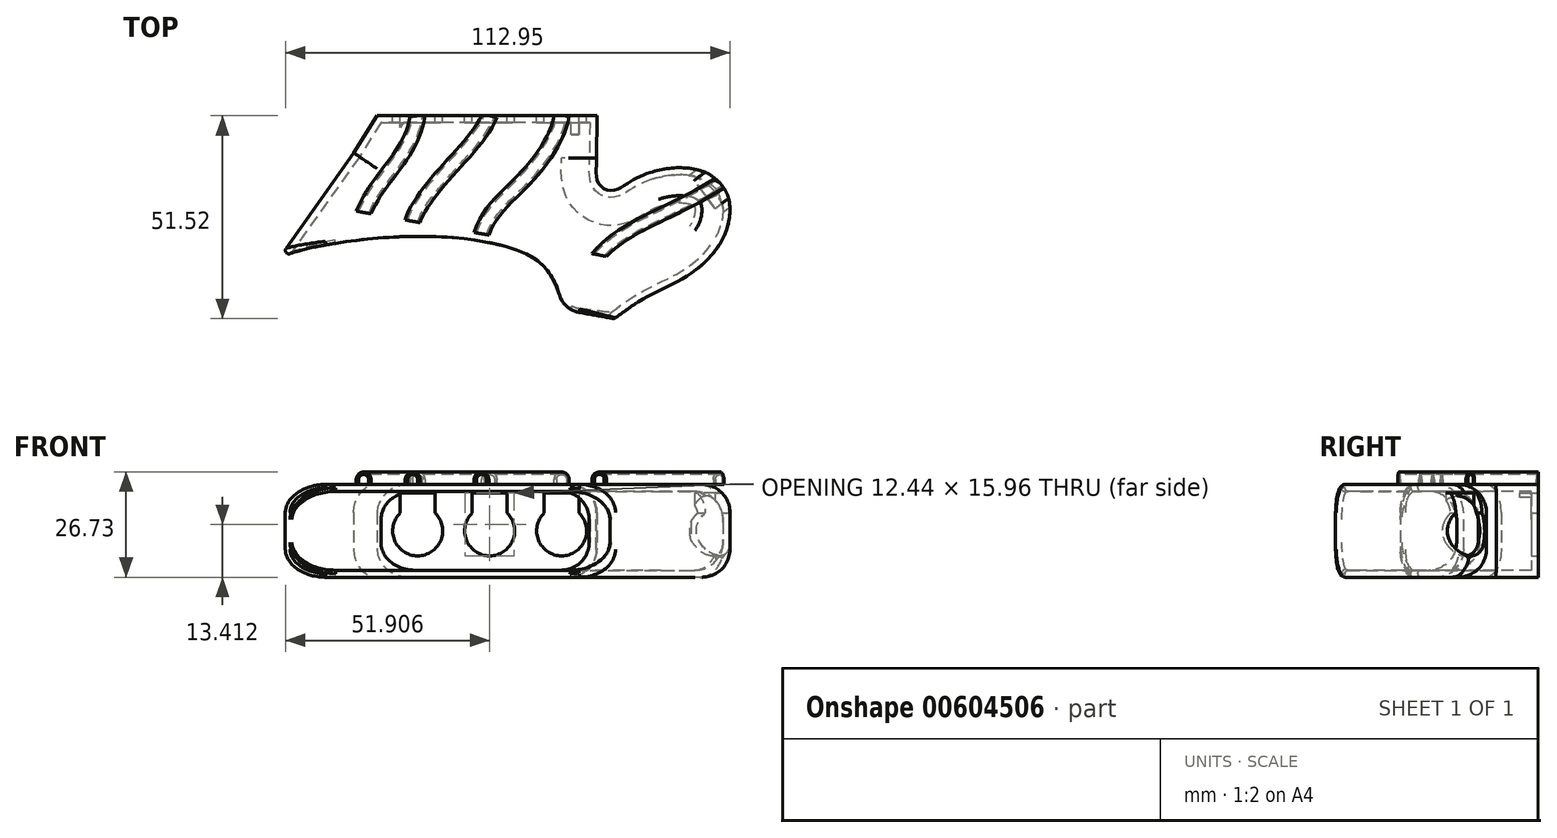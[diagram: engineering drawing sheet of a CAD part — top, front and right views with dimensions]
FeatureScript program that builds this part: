
annotation { "Feature Type Name" : "Feature", "Feature Type Description" : "" }
export const myFeature = defineFeature(function(context is Context, id is Id, definition is map)
    precondition{}
    {
        {
            var Q0;
            Q0=qCreatedBy(makeId("Top.planeOp"),FACE);
            var sketch = newSketch(context, id + "F0", { "sketchPlane" : qUnion([Q0])});
            skLineSegment(sketch, "E0", {"start": v(-2.53, 3.76) * mm, "end": v(-21.5, -22.97) * mm});
            skLineSegment(sketch, "E1", {"start": v(54.7, -36.74) * mm, "end": v(63.69, -38.36) * mm});
            skFitSpline(sketch, "E2", {"points": [v(54.7, 11.38) * mm, v(59, 4.04) * mm, v(59.53, -3.66) * mm, v(63.11, -5.79) * mm, v(68.43, -3.13) * mm, v(80.08, 0) * mm, v(90.97, -4.14) * mm, v(92.29, -15.51) * mm, v(83.28, -26.78) * mm, v(72.06, -32.72) * mm, v(63.69, -38.36) * mm], "startDerivative": vector(65.3, -76.98) * mm, "endDerivative": vector(-77.9, -55.9) * mm});
            skLineSegment(sketch, "E3", {"start": v(59.3, 13.2) * mm, "end": v(3.43, 13.2) * mm});
            skLineSegment(sketch, "E4", {"start": v(3.43, 13.2) * mm, "end": v(-2.53, 3.76) * mm});
            skLineSegment(sketch, "E5", {"start": v(59.3, 13.2) * mm, "end": v(59.13, 2.47) * mm});
            skLineSegment(sketch, "E6", {"start": v(84.86, 3.75) * mm, "end": v(96.23, -11.53) * mm});
            skLineSegment(sketch, "E7", {"start": v(84.86, 3.75) * mm, "end": v(72.77, -1.24) * mm});
            skLineSegment(sketch, "E8", {"start": v(96.23, -11.53) * mm, "end": v(90.2, -19.8) * mm});
            skFitSpline(sketch, "E9", {"points": [v(-21.5, -22.97) * mm, v(-10.47, -19.77) * mm, v(16.08, -17.45) * mm, v(40.88, -21.74) * mm, v(47.96, -28) * mm, v(50.62, -36) * mm], "startDerivative": vector(55.83, 25.77) * mm, "endDerivative": vector(10.05, -54.75) * mm});
            skArc(sketch, "E10.filletArc", {"start": v(49.75, -32.32) * mm, "mid": v(51.6, -35.23) * mm, "end": v(54.7, -36.74) * mm});
            skSolve(sketch);
        }
        {
            var Q0;
            Q0=makeQuery(id+"F0.imprint","IMPRINT",FACE,{"disambiguationData":[TD([[makeQuery(id+"F0.imprint","IMPRINT",EDGE,{"derivedFrom":sQuery(id+"F0.wireOp",EDGE,"E0")}),1.0]])]});
            extrude(context, id + "F1", {"entities" : qUnion([Q0]), "depth" : 23.56 * mm, "offsetDistance" : 25.4 * mm});
        }
        {
            var Q0;
            Q0=makeQuery(id+"F1.opExtrude","SWEPT_FACE",FACE,{"disambiguationData":[OSD([sQuery(id+"F0.wireOp",EDGE,"E1")])]});
            var Q1;
            Q1=makeQuery(id+"F1.opExtrude","SWEPT_FACE",FACE,{"disambiguationData":[OSD([sQuery(id+"F0.wireOp",EDGE,"E9")])]});
            var Q2;
            Q2=makeQuery(id+"F1.opExtrude","SWEPT_FACE",FACE,{"disambiguationData":[OSD([sQuery(id+"F0.wireOp",EDGE,"E10.filletArc")])]});
            shell(context, id + "F2", {"entities" : qUnion([Q0, Q1, Q2]), "thickness" : 1.78 * mm});
        }
        {
            var Q0;
            {var subQ0=sQuery(id+"F0.wireOp",EDGE,"E2");Q0=makeQuery(id+"F2.opShell","OFFSET_EDGE",EDGE,{"disambiguationData":[OSD([subQ0]),TDD([makeQuery(id+"F1.opExtrude","CAP_EDGE",EDGE,{"disambiguationData":[OSD([subQ0])],"isStart":false})])]});}
            var Q1;
            {var subQ0=sQuery(id+"F0.wireOp",EDGE,"E0");Q1=makeQuery(id+"F2.opShell","OFFSET_EDGE",EDGE,{"disambiguationData":[OSD([subQ0]),TDD([makeQuery(id+"F1.opExtrude","CAP_EDGE",EDGE,{"disambiguationData":[OSD([subQ0])],"isStart":true})])]});}
            var Q2;
            {var subQ0=sQuery(id+"F0.wireOp",EDGE,"E0");Q2=makeQuery(id+"F2.opShell","OFFSET_EDGE",EDGE,{"disambiguationData":[OSD([subQ0]),TDD([makeQuery(id+"F1.opExtrude","CAP_EDGE",EDGE,{"disambiguationData":[OSD([subQ0])],"isStart":false})])]});}
            var Q3;
            Q3=makeQuery(id+"F2.opShell","OFFSET_EDGE",EDGE,{"disambiguationData":[OSD([sQuery(id+"F0.wireOp",EDGE,"E0"),sQuery(id+"F0.wireOp",EDGE,"E4")])]});
            var Q4;
            {var subQ0=sQuery(id+"F0.wireOp",EDGE,"E4");Q4=makeQuery(id+"F2.opShell","OFFSET_EDGE",EDGE,{"disambiguationData":[OSD([subQ0]),TDD([makeQuery(id+"F1.opExtrude","CAP_EDGE",EDGE,{"disambiguationData":[OSD([subQ0])],"isStart":false})])]});}
            var Q5;
            {var subQ0=sQuery(id+"F0.wireOp",EDGE,"E4");Q5=makeQuery(id+"F2.opShell","OFFSET_EDGE",EDGE,{"disambiguationData":[OSD([subQ0]),TDD([makeQuery(id+"F1.opExtrude","CAP_EDGE",EDGE,{"disambiguationData":[OSD([subQ0])],"isStart":true})])]});}
            var Q6;
            Q6=makeQuery(id+"F1.opExtrude","CAP_EDGE",EDGE,{"disambiguationData":[OSD([sQuery(id+"F0.wireOp",EDGE,"E2")])],"isStart":false});
            var Q7;
            Q7=makeQuery(id+"F1.opExtrude","CAP_EDGE",EDGE,{"disambiguationData":[OSD([sQuery(id+"F0.wireOp",EDGE,"E0")])],"isStart":false});
            var Q8;
            Q8=makeQuery(id+"F1.opExtrude","CAP_EDGE",EDGE,{"disambiguationData":[OSD([sQuery(id+"F0.wireOp",EDGE,"E4")])],"isStart":false});
            var Q9;
            Q9=makeQuery(id+"F1.opExtrude","CAP_EDGE",EDGE,{"disambiguationData":[OSD([sQuery(id+"F0.wireOp",EDGE,"E2")])],"isStart":true});
            var Q10;
            Q10=makeQuery(id+"F1.opExtrude","CAP_EDGE",EDGE,{"disambiguationData":[OSD([sQuery(id+"F0.wireOp",EDGE,"E0")])],"isStart":true});
            var Q11;
            Q11=makeQuery(id+"F1.opExtrude","CAP_EDGE",EDGE,{"disambiguationData":[OSD([sQuery(id+"F0.wireOp",EDGE,"E5")])],"isStart":false});
            var Q12;
            Q12=makeQuery(id+"F1.opExtrude","CAP_EDGE",EDGE,{"disambiguationData":[OSD([sQuery(id+"F0.wireOp",EDGE,"E5")])],"isStart":true});
            var Q13;
            {var subQ0=sQuery(id+"F0.wireOp",EDGE,"E5");Q13=makeQuery(id+"F2.opShell","OFFSET_EDGE",EDGE,{"disambiguationData":[OSD([subQ0]),TDD([makeQuery(id+"F1.opExtrude","CAP_EDGE",EDGE,{"disambiguationData":[OSD([subQ0])],"isStart":false})])]});}
            var Q14;
            {var subQ0=sQuery(id+"F0.wireOp",EDGE,"E5");Q14=makeQuery(id+"F2.opShell","OFFSET_EDGE",EDGE,{"disambiguationData":[OSD([subQ0]),TDD([makeQuery(id+"F1.opExtrude","CAP_EDGE",EDGE,{"disambiguationData":[OSD([subQ0])],"isStart":true})])]});}
            var Q15;
            Q15=makeQuery(id+"F1.opExtrude","CAP_EDGE",EDGE,{"disambiguationData":[OSD([sQuery(id+"F0.wireOp",EDGE,"E4")])],"isStart":true});
            var Q16;
            {var subQ0=sQuery(id+"F0.wireOp",EDGE,"E2");Q16=makeQuery(id+"F2.opShell","OFFSET_EDGE",EDGE,{"disambiguationData":[OSD([subQ0]),TDD([makeQuery(id+"F1.opExtrude","CAP_EDGE",EDGE,{"disambiguationData":[OSD([subQ0])],"isStart":false})])]});}
            var Q17;
            {var subQ0=sQuery(id+"F0.wireOp",EDGE,"E8");Q17=makeQuery(id+"F2.opShell","OFFSET_EDGE",EDGE,{"disambiguationData":[OSD([subQ0]),TDD([makeQuery(id+"F1.opExtrude","CAP_EDGE",EDGE,{"disambiguationData":[OSD([subQ0])],"isStart":false})])]});}
            var Q18;
            {var subQ0=sQuery(id+"F0.wireOp",EDGE,"E2");Q18=makeQuery(id+"F2.opShell","OFFSET_EDGE",EDGE,{"disambiguationData":[OSD([subQ0]),TDD([makeQuery(id+"F1.opExtrude","CAP_EDGE",EDGE,{"disambiguationData":[OSD([subQ0])],"isStart":true})])]});}
            var Q19;
            {var subQ0=sQuery(id+"F0.wireOp",EDGE,"E8");Q19=makeQuery(id+"F2.opShell","OFFSET_EDGE",EDGE,{"disambiguationData":[OSD([subQ0]),TDD([makeQuery(id+"F1.opExtrude","CAP_EDGE",EDGE,{"disambiguationData":[OSD([subQ0])],"isStart":true})])]});}
            var Q20;
            {var subQ0=sQuery(id+"F0.wireOp",EDGE,"E7");Q20=makeQuery(id+"F2.opShell","OFFSET_EDGE",EDGE,{"disambiguationData":[OSD([subQ0]),TDD([makeQuery(id+"F1.opExtrude","CAP_EDGE",EDGE,{"disambiguationData":[OSD([subQ0])],"isStart":false})])]});}
            var Q21;
            {var subQ0=sQuery(id+"F0.wireOp",EDGE,"E7");Q21=makeQuery(id+"F2.opShell","OFFSET_EDGE",EDGE,{"disambiguationData":[OSD([subQ0]),TDD([makeQuery(id+"F1.opExtrude","CAP_EDGE",EDGE,{"disambiguationData":[OSD([subQ0])],"isStart":true})])]});}
            var Q22;
            Q22=makeQuery(id+"F1.opExtrude","CAP_EDGE",EDGE,{"disambiguationData":[OSD([sQuery(id+"F0.wireOp",EDGE,"E7")])],"isStart":true});
            var Q23;
            Q23=makeQuery(id+"F1.opExtrude","CAP_EDGE",EDGE,{"disambiguationData":[OSD([sQuery(id+"F0.wireOp",EDGE,"E2")])],"isStart":false});
            var Q24;
            Q24=makeQuery(id+"F1.opExtrude","CAP_EDGE",EDGE,{"disambiguationData":[OSD([sQuery(id+"F0.wireOp",EDGE,"E8")])],"isStart":false});
            var Q25;
            Q25=makeQuery(id+"F1.opExtrude","CAP_EDGE",EDGE,{"disambiguationData":[OSD([sQuery(id+"F0.wireOp",EDGE,"E8")])],"isStart":true});
            var Q26;
            Q26=makeQuery(id+"F1.opExtrude","CAP_EDGE",EDGE,{"disambiguationData":[OSD([sQuery(id+"F0.wireOp",EDGE,"E2")])],"isStart":true});
            var Q27;
            Q27=makeQuery(id+"F1.opExtrude","CAP_EDGE",EDGE,{"disambiguationData":[OSD([sQuery(id+"F0.wireOp",EDGE,"E7")])],"isStart":false});
            fillet(context, id + "F3", {"entities" : qUnion([Q0, Q1, Q2, Q3, Q4, Q5, Q6, Q7, Q8, Q9, Q10, Q11, Q12, Q13, Q14, Q15, Q16, Q17, Q18, Q19, Q20, Q21, Q22, Q23, Q24, Q25, Q26, Q27]), "radius" : 7.11 * mm, "tangentPropagation" : true, "allowEdgeOverflow" : false});
        }
        {
            var Q0;
            Q0=makeQuery(id+"F1.opExtrude","SWEPT_FACE",FACE,{"disambiguationData":[OSD([sQuery(id+"F0.wireOp",EDGE,"E3")])]});
            var sketch = newSketch(context, id + "F4", { "sketchPlane" : qUnion([Q0])});
            skCircle(sketch, "E11", {"center": v(-32.02, 11.78) * mm, "radius": 6.35 * mm});
            skCircle(sketch, "E12", {"center": v(-50.3, 11.78) * mm, "radius": 6.35 * mm});
            skCircle(sketch, "E13.MirrorC", {"center": v(-13.73, 11.78) * mm, "radius": 6.35 * mm});
            skLineSegment(sketch, "E14", {"start": v(-32.02, 0) * mm, "end": v(-32.02, 23.56) * mm});
            skSolve(sketch);
        }
        {
            var Q0;
            Q0=qSketchRegion(id+"F4",true);
            extrude(context, id + "F5", {"entities" : qUnion([Q0]), "operationType" : NewBodyOperationType.REMOVE, "endBound" : BoundingType.THROUGH_ALL, "oppositeDirection" : true, "depth" : 25.4 * mm, "offsetDistance" : 25.4 * mm});
        }
        {
            var Q0;
            Q0=makeQuery(id+"F1.opExtrude","SWEPT_FACE",FACE,{"disambiguationData":[OSD([sQuery(id+"F0.wireOp",EDGE,"E3")])]});
            var sketch = newSketch(context, id + "F6", { "sketchPlane" : qUnion([Q0])});
            skLineSegment(sketch, "E15", {"start": v(-32.02, 23.56) * mm, "end": v(-32.02, 0) * mm});
            skLineSegment(sketch, "E16", {"start": v(-32.02, 21.4) * mm, "end": v(-27.57, 21.4) * mm});
            skLineSegment(sketch, "E17", {"start": v(-27.57, 21.4) * mm, "end": v(-27.57, 16.31) * mm});
            skArc(sketch, "E18", {"start": v(-32.02, 18.13) * mm, "mid": v(-29.62, 17.66) * mm, "end": v(-27.57, 16.31) * mm});
            skArc(sketch, "E19.MirrorCS", {"start": v(-32.02, 18.13) * mm, "mid": v(-34.42, 17.66) * mm, "end": v(-36.46, 16.31) * mm});
            skLineSegment(sketch, "E20.MirrorCS", {"start": v(-32.02, 21.4) * mm, "end": v(-36.46, 21.4) * mm});
            skLineSegment(sketch, "E21.MirrorCS", {"start": v(-36.46, 21.4) * mm, "end": v(-36.46, 16.31) * mm});
            skLineSegment(sketch, "E22", {"start": v(-50.3, 21.4) * mm, "end": v(-45.86, 21.4) * mm});
            skLineSegment(sketch, "E23", {"start": v(-45.86, 21.4) * mm, "end": v(-45.86, 16.31) * mm});
            skArc(sketch, "E24", {"start": v(-50.3, 18.13) * mm, "mid": v(-47.9, 17.66) * mm, "end": v(-45.86, 16.31) * mm});
            skArc(sketch, "E25.MirrorCS", {"start": v(-50.3, 18.13) * mm, "mid": v(-52.7, 17.66) * mm, "end": v(-54.75, 16.31) * mm});
            skLineSegment(sketch, "E26.MirrorCS", {"start": v(-50.3, 21.4) * mm, "end": v(-54.75, 21.4) * mm});
            skLineSegment(sketch, "E27.MirrorCS", {"start": v(-54.75, 21.4) * mm, "end": v(-54.75, 16.31) * mm});
            skLineSegment(sketch, "E28", {"start": v(-13.73, 21.4) * mm, "end": v(-9.28, 21.4) * mm});
            skLineSegment(sketch, "E29", {"start": v(-9.28, 21.4) * mm, "end": v(-9.28, 16.31) * mm});
            skArc(sketch, "E30", {"start": v(-13.73, 18.13) * mm, "mid": v(-11.33, 17.66) * mm, "end": v(-9.28, 16.31) * mm});
            skArc(sketch, "E31.MirrorCS", {"start": v(-13.73, 18.13) * mm, "mid": v(-16.13, 17.66) * mm, "end": v(-18.17, 16.31) * mm});
            skLineSegment(sketch, "E32.MirrorCS", {"start": v(-13.73, 21.4) * mm, "end": v(-18.17, 21.4) * mm});
            skLineSegment(sketch, "E33.MirrorCS", {"start": v(-18.17, 21.4) * mm, "end": v(-18.17, 16.31) * mm});
            skSolve(sketch);
        }
        {
            var Q0;
            Q0=qSketchRegion(id+"F6",true);
            extrude(context, id + "F7", {"entities" : qUnion([Q0]), "operationType" : NewBodyOperationType.REMOVE, "oppositeDirection" : true, "depth" : 4.83 * mm, "offsetDistance" : 25.4 * mm});
        }
        {
            var Q0;
            Q0=makeQuery(id+"F1.opExtrude","SWEPT_FACE",FACE,{"disambiguationData":[OSD([sQuery(id+"F0.wireOp",EDGE,"E6")])]});
            var sketch = newSketch(context, id + "F8", { "sketchPlane" : qUnion([Q0])});
            skCircle(sketch, "E34", {"center": v(-57.18, 11.78) * mm, "radius": 6.35 * mm});
            skLineSegment(sketch, "E35", {"start": v(-57.18, 21.4) * mm, "end": v(-52.74, 21.4) * mm});
            skLineSegment(sketch, "E36", {"start": v(-52.74, 21.4) * mm, "end": v(-52.74, 16.31) * mm});
            skLineSegment(sketch, "E37.MirrorCS", {"start": v(-57.18, 21.4) * mm, "end": v(-61.63, 21.4) * mm});
            skLineSegment(sketch, "E38.MirrorCS", {"start": v(-61.63, 21.4) * mm, "end": v(-61.63, 16.31) * mm});
            skSolve(sketch);
        }
        {
            var Q0;
            Q0 = qSketchRegion(id + "F8", true);
            var Q1;
            Q1=makeQuery(id+"F8.imprint","IMPRINT",FACE,{"disambiguationData":[TD([[makeQuery(id+"F8.imprint","IMPRINT",EDGE,{"derivedFrom":sQuery(id+"F8.wireOp",EDGE,"E35")}),-1.0]])]});
            var Q2;
            {var subQ0=sQuery(id+"F8.wireOp",EDGE,"E34");var subQ1=makeQuery(id+"F8.imprint","INTERSECT",VERTEX,{"derivedFrom":[subQ0,sQuery(id+"F8.wireOp",EDGE,"E36")]});Q2=makeQuery(id+"F8.imprint","IMPRINT",FACE,{"disambiguationData":[TD([[makeQuery(id+"F8.imprint","IMPRINT",EDGE,{"disambiguationData":[TD([[subQ1,-1.0]])],"derivedFrom":subQ0}),1.0]])]});}
            extrude(context, id + "F9", {"entities" : qUnion([Q0, Q1, Q2]), "operationType" : NewBodyOperationType.REMOVE, "oppositeDirection" : true, "depth" : 4.83 * mm, "offsetDistance" : 25.4 * mm});
        }
        {
            var Q0;
            Q0=makeQuery(id+"F1.opExtrude","CAP_FACE",FACE,{"disambiguationData":[OSD([sQuery(id+"F0.wireOp",EDGE,"E0"),sQuery(id+"F0.wireOp",EDGE,"E1"),sQuery(id+"F0.wireOp",EDGE,"E2"),sQuery(id+"F0.wireOp",EDGE,"E3"),sQuery(id+"F0.wireOp",EDGE,"E4"),sQuery(id+"F0.wireOp",EDGE,"E5"),sQuery(id+"F0.wireOp",EDGE,"E6"),sQuery(id+"F0.wireOp",EDGE,"E7"),sQuery(id+"F0.wireOp",EDGE,"E8"),sQuery(id+"F0.wireOp",EDGE,"E2"),sQuery(id+"F0.wireOp",EDGE,"E9"),sQuery(id+"F0.wireOp",EDGE,"E10.filletArc")])],"isStart":false});
            var sketch = newSketch(context, id + "F10", { "sketchPlane" : qUnion([Q0])});
            skPoint(sketch, "E39.0", {"position": v(-1.92, -11.02) * mm});
            skPoint(sketch, "E40.0", {"position": v(61.78, -22.53) * mm});
            skLineSegment(sketch, "E41", {"start": v(-1.92, -11.02) * mm, "end": v(61.78, -22.53) * mm});
            skPoint(sketch, "E42.0", {"position": v(13.73, 13.2) * mm});
            skPoint(sketch, "E43.0", {"position": v(32.02, 13.2) * mm});
            skPoint(sketch, "E44.0", {"position": v(50.3, 13.2) * mm});
            skPoint(sketch, "E45.0", {"position": v(90.54, -3.89) * mm});
            skFitSpline(sketch, "E46", {"points": [v(13.73, 13.2) * mm, v(7.28, 0) * mm, v(0, -11.37) * mm], "startDerivative": vector(-4.34, -30.73) * mm, "endDerivative": vector(-13.54, -30.47) * mm});
            skPoint(sketch, "E47.0", {"position": v(12.45, -13.62) * mm});
            skPoint(sketch, "E48.0", {"position": v(29.95, -16.78) * mm});
            skFitSpline(sketch, "E49", {"points": [v(32.02, 13.2) * mm, v(21.18, -0.88) * mm, v(12.45, -13.62) * mm], "startDerivative": vector(-10.72, -26.08) * mm, "endDerivative": vector(-7.14, -23.27) * mm});
            skFitSpline(sketch, "E50", {"points": [v(50.3, 13.2) * mm, v(41.19, -2.5) * mm, v(29.95, -16.78) * mm], "startDerivative": vector(-5.49, -32.55) * mm, "endDerivative": vector(-12.27, -36.66) * mm});
            skFitSpline(sketch, "E51", {"points": [v(90.54, -3.89) * mm, v(72.14, -13.57) * mm, v(59.87, -22.19) * mm], "startDerivative": vector(-34.13, -21.6) * mm, "endDerivative": vector(-22.86, -25.58) * mm});
            skSolve(sketch);
        }
        {
            var Q0;
            Q0=sQuery(id+"F10.wireOp",EDGE,"E41");
            cPlane(context, id + "F11", {"entities" : qUnion([Q0]), "cplaneType" : CPlaneType.LINE_ANGLE, "offset" : 25.4 * mm, "angle" : 0 * degree, "width" : 152.4 * mm, "height" : 152.4 * mm});
        }
        {
            var Q0;
            Q0=qCreatedBy(id+"F11.planeOp",FACE);
            var sketch = newSketch(context, id + "F12", { "sketchPlane" : qUnion([Q0])});
            skPoint(sketch, "E52.0", {"position": v(-2.02, 23.56) * mm});
            skPoint(sketch, "E53.0", {"position": v(-14.67, 23.56) * mm});
            skPoint(sketch, "E54.0", {"position": v(-32.45, 23.56) * mm});
            skPoint(sketch, "E55.0", {"position": v(-62.86, 23.56) * mm});
            skLineSegment(sketch, "E56", {"start": v(-0.12, 24.83) * mm, "end": v(-0.12, 23.56) * mm});
            skLineSegment(sketch, "E57", {"start": v(-0.12, 23.56) * mm, "end": v(-3.93, 23.56) * mm});
            skLineSegment(sketch, "E58", {"start": v(-3.93, 23.56) * mm, "end": v(-3.93, 24.83) * mm});
            skLineSegment(sketch, "E59", {"start": v(-12.77, 24.83) * mm, "end": v(-12.77, 23.56) * mm});
            skLineSegment(sketch, "E60", {"start": v(-12.77, 23.56) * mm, "end": v(-16.58, 23.56) * mm});
            skLineSegment(sketch, "E61", {"start": v(-16.58, 23.56) * mm, "end": v(-16.58, 24.83) * mm});
            skLineSegment(sketch, "E62", {"start": v(-30.55, 24.83) * mm, "end": v(-30.55, 23.56) * mm});
            skLineSegment(sketch, "E63", {"start": v(-30.55, 23.56) * mm, "end": v(-34.36, 23.56) * mm});
            skLineSegment(sketch, "E64", {"start": v(-34.36, 23.56) * mm, "end": v(-34.36, 24.83) * mm});
            skLineSegment(sketch, "E65", {"start": v(-60.96, 24.83) * mm, "end": v(-60.96, 23.56) * mm});
            skLineSegment(sketch, "E66", {"start": v(-60.96, 23.56) * mm, "end": v(-64.77, 23.56) * mm});
            skLineSegment(sketch, "E67", {"start": v(-64.77, 23.56) * mm, "end": v(-64.77, 24.83) * mm});
            skArc(sketch, "E68", {"start": v(-60.96, 24.83) * mm, "mid": v(-62.86, 26.73) * mm, "end": v(-64.77, 24.83) * mm});
            skArc(sketch, "E69", {"start": v(-30.55, 24.83) * mm, "mid": v(-32.45, 26.73) * mm, "end": v(-34.36, 24.83) * mm});
            skArc(sketch, "E70", {"start": v(-12.77, 24.83) * mm, "mid": v(-14.67, 26.73) * mm, "end": v(-16.58, 24.83) * mm});
            skArc(sketch, "E71", {"start": v(-0.12, 24.83) * mm, "mid": v(-2.02, 26.73) * mm, "end": v(-3.93, 24.83) * mm});
            skLineSegment(sketch, "E72", {"start": v(-0.75, 24.83) * mm, "end": v(-0.75, 23.56) * mm});
            skLineSegment(sketch, "E73", {"start": v(-3.3, 24.83) * mm, "end": v(-3.3, 23.56) * mm});
            skArc(sketch, "E74", {"start": v(-0.75, 24.83) * mm, "mid": v(-2.02, 26.1) * mm, "end": v(-3.3, 24.83) * mm});
            skArc(sketch, "E75", {"start": v(-13.4, 24.83) * mm, "mid": v(-14.67, 26.1) * mm, "end": v(-15.94, 24.83) * mm});
            skArc(sketch, "E76", {"start": v(-31.18, 24.83) * mm, "mid": v(-32.45, 26.1) * mm, "end": v(-33.72, 24.83) * mm});
            skArc(sketch, "E77", {"start": v(-61.6, 24.83) * mm, "mid": v(-62.86, 26.1) * mm, "end": v(-64.13, 24.83) * mm});
            skLineSegment(sketch, "E78", {"start": v(-64.13, 24.83) * mm, "end": v(-64.13, 23.56) * mm});
            skLineSegment(sketch, "E79", {"start": v(-61.6, 24.83) * mm, "end": v(-61.6, 23.56) * mm});
            skLineSegment(sketch, "E80", {"start": v(-33.72, 24.83) * mm, "end": v(-33.72, 23.56) * mm});
            skLineSegment(sketch, "E81", {"start": v(-31.18, 24.83) * mm, "end": v(-31.18, 23.56) * mm});
            skLineSegment(sketch, "E82", {"start": v(-15.94, 24.83) * mm, "end": v(-15.94, 23.56) * mm});
            skLineSegment(sketch, "E83", {"start": v(-13.4, 24.83) * mm, "end": v(-13.4, 23.56) * mm});
            skSolve(sketch);
        }
        {
            var Q0;
            {var subQ3=sQuery(id+"F12.wireOp",EDGE,"E56");Q0=makeQuery(id+"F12.imprint","IMPRINT",FACE,{"disambiguationData":[TD([[makeQuery(id+"F12.imprint","IMPRINT",EDGE,{"derivedFrom":subQ3}),-1.0]])]});}
            var Q1;
            Q1=sQuery(id+"F10.wireOp",EDGE,"E46");
            sweep(context, id + "F13", {"operationType" : NewBodyOperationType.ADD, "profiles" : qUnion([Q0]), "path" : qUnion([Q1])});
        }
        {
            var Q0;
            {var subQ3=sQuery(id+"F12.wireOp",EDGE,"E59");Q0=makeQuery(id+"F12.imprint","IMPRINT",FACE,{"disambiguationData":[TD([[makeQuery(id+"F12.imprint","IMPRINT",EDGE,{"derivedFrom":subQ3}),-1.0]])]});}
            var Q1;
            Q1=sQuery(id+"F10.wireOp",EDGE,"E49");
            sweep(context, id + "F14", {"operationType" : NewBodyOperationType.ADD, "profiles" : qUnion([Q0]), "path" : qUnion([Q1])});
        }
        {
            var Q0;
            {var subQ3=sQuery(id+"F12.wireOp",EDGE,"E62");Q0=makeQuery(id+"F12.imprint","IMPRINT",FACE,{"disambiguationData":[TD([[makeQuery(id+"F12.imprint","IMPRINT",EDGE,{"derivedFrom":subQ3}),-1.0]])]});}
            var Q1;
            Q1=sQuery(id+"F10.wireOp",EDGE,"E50");
            sweep(context, id + "F15", {"operationType" : NewBodyOperationType.ADD, "profiles" : qUnion([Q0]), "path" : qUnion([Q1])});
        }
        {
            var Q0;
            {var subQ3=sQuery(id+"F12.wireOp",EDGE,"E65");Q0=makeQuery(id+"F12.imprint","IMPRINT",FACE,{"disambiguationData":[TD([[makeQuery(id+"F12.imprint","IMPRINT",EDGE,{"derivedFrom":subQ3}),-1.0]])]});}
            var Q1;
            Q1=sQuery(id+"F10.wireOp",EDGE,"E51");
            sweep(context, id + "F16", {"operationType" : NewBodyOperationType.ADD, "profiles" : qUnion([Q0]), "path" : qUnion([Q1])});
        }
        {
            var Q0;
            Q0=makeQuery(id+"F1.opExtrude","CAP_FACE",FACE,{"disambiguationData":[OSD([sQuery(id+"F0.wireOp",EDGE,"E0"),sQuery(id+"F0.wireOp",EDGE,"E1"),sQuery(id+"F0.wireOp",EDGE,"E2"),sQuery(id+"F0.wireOp",EDGE,"E3"),sQuery(id+"F0.wireOp",EDGE,"E4"),sQuery(id+"F0.wireOp",EDGE,"E5"),sQuery(id+"F0.wireOp",EDGE,"E6"),sQuery(id+"F0.wireOp",EDGE,"E7"),sQuery(id+"F0.wireOp",EDGE,"E8"),sQuery(id+"F0.wireOp",EDGE,"E2"),sQuery(id+"F0.wireOp",EDGE,"E9"),sQuery(id+"F0.wireOp",EDGE,"E10.filletArc")])],"isStart":false});
            var sketch = newSketch(context, id + "F17", { "sketchPlane" : qUnion([Q0])});
            skPoint(sketch, "E84.0", {"position": v(13.73, 13.2) * mm});
            skPoint(sketch, "E85.0", {"position": v(50.3, 13.2) * mm});
            skPoint(sketch, "E86.0", {"position": v(90.54, -3.89) * mm});
            skPoint(sketch, "E87.0", {"position": v(91.52, -5.2) * mm});
            skPoint(sketch, "E88.0", {"position": v(92.25, -4.73) * mm});
            skPoint(sketch, "E89.0", {"position": v(30.18, 13.72) * mm});
            skLineSegment(sketch, "E90", {"start": v(50.3, 13.2) * mm, "end": v(30.18, 13.72) * mm});
            skPoint(sketch, "E91.0", {"position": v(15.62, 13.4) * mm});
            skLineSegment(sketch, "E92", {"start": v(30.18, 13.72) * mm, "end": v(15.62, 13.4) * mm});
            skLineSegment(sketch, "E93", {"start": v(13.73, 13.2) * mm, "end": v(50.3, 13.2) * mm});
            skLineSegment(sketch, "E94", {"start": v(15.62, 13.4) * mm, "end": v(13.73, 13.2) * mm});
            skLineSegment(sketch, "E95", {"start": v(91.52, -5.2) * mm, "end": v(92.25, -4.73) * mm});
            skLineSegment(sketch, "E96", {"start": v(92.25, -4.73) * mm, "end": v(90.54, -3.89) * mm});
            skLineSegment(sketch, "E97", {"start": v(90.54, -3.89) * mm, "end": v(91.52, -5.2) * mm});
            skSolve(sketch);
        }
        {
            var Q0;
            Q0 = qSketchRegion(id + "F17", true);
            extrude(context, id + "F18", {"entities" : qUnion([Q0]), "operationType" : NewBodyOperationType.REMOVE, "endBound" : BoundingType.THROUGH_ALL, "oppositeDirection" : true, "depth" : 25.4 * mm, "offsetDistance" : 25.4 * mm, "hasSecondDirection" : true, "secondDirectionBound" : SecondDirectionBoundingType.THROUGH_ALL, "secondDirectionOppositeDirection" : false, "secondDirectionDepth" : 25.4 * mm});
        }
        {
            var Q0;
            Q0=makeQuery(id+"F1.opExtrude","CAP_EDGE",EDGE,{"disambiguationData":[OSD([sQuery(id+"F0.wireOp",EDGE,"E9")])],"isStart":false});
            var Q1;
            Q1=makeQuery(id+"F3.opFillet","BLEND_EDGE",EDGE,{"blendedFrom":[makeQuery(id+"F1.opExtrude","CAP_EDGE",EDGE,{"disambiguationData":[OSD([sQuery(id+"F0.wireOp",EDGE,"E0")])],"isStart":false}),makeQuery(id+"F1.opExtrude","SWEPT_FACE",FACE,{"disambiguationData":[OSD([sQuery(id+"F0.wireOp",EDGE,"E9")])]})],"blendedInto":[makeQuery(id+"F1.opExtrude","SWEPT_FACE",FACE,{"disambiguationData":[OSD([sQuery(id+"F0.wireOp",EDGE,"E9")])]})]});
            var Q2;
            Q2=makeQuery(id+"F1.opExtrude","SWEPT_EDGE",EDGE,{"disambiguationData":[OSD([sQuery(id+"F0.wireOp",EDGE,"E0"),sQuery(id+"F0.wireOp",EDGE,"E9")])]});
            var Q3;
            Q3=makeQuery(id+"F3.opFillet","BLEND_EDGE",EDGE,{"blendedFrom":[makeQuery(id+"F1.opExtrude","CAP_EDGE",EDGE,{"disambiguationData":[OSD([sQuery(id+"F0.wireOp",EDGE,"E0")])],"isStart":true}),makeQuery(id+"F1.opExtrude","SWEPT_FACE",FACE,{"disambiguationData":[OSD([sQuery(id+"F0.wireOp",EDGE,"E9")])]})],"blendedInto":[makeQuery(id+"F1.opExtrude","SWEPT_FACE",FACE,{"disambiguationData":[OSD([sQuery(id+"F0.wireOp",EDGE,"E9")])]})]});
            var Q4;
            Q4=makeQuery(id+"F1.opExtrude","CAP_EDGE",EDGE,{"disambiguationData":[OSD([sQuery(id+"F0.wireOp",EDGE,"E9")])],"isStart":true});
            var Q5;
            Q5=makeQuery(id+"F1.opExtrude","CAP_EDGE",EDGE,{"disambiguationData":[OSD([sQuery(id+"F0.wireOp",EDGE,"E10.filletArc")])],"isStart":true});
            var Q6;
            Q6=makeQuery(id+"F3.opFillet","BLEND_EDGE",EDGE,{"blendedFrom":[makeQuery(id+"F1.opExtrude","CAP_EDGE",EDGE,{"disambiguationData":[OSD([sQuery(id+"F0.wireOp",EDGE,"E2")])],"isStart":true}),makeQuery(id+"F2.opShell","OFFSET_FACE",FACE,{"disambiguationData":[OSD([sQuery(id+"F0.wireOp",EDGE,"E10.filletArc")])]})],"blendedInto":[makeQuery(id+"F2.opShell","OFFSET_FACE",FACE,{"disambiguationData":[OSD([sQuery(id+"F0.wireOp",EDGE,"E10.filletArc")])]})]});
            var Q7;
            Q7=makeQuery(id+"F3.opFillet","BLEND_EDGE",EDGE,{"blendedFrom":[makeQuery(id+"F1.opExtrude","CAP_EDGE",EDGE,{"disambiguationData":[OSD([sQuery(id+"F0.wireOp",EDGE,"E2")])],"isStart":true}),makeQuery(id+"F1.opExtrude","SWEPT_FACE",FACE,{"disambiguationData":[OSD([sQuery(id+"F0.wireOp",EDGE,"E1")])]})],"blendedInto":[makeQuery(id+"F1.opExtrude","SWEPT_FACE",FACE,{"disambiguationData":[OSD([sQuery(id+"F0.wireOp",EDGE,"E1")])]})]});
            var Q8;
            Q8=makeQuery(id+"F1.opExtrude","SWEPT_EDGE",EDGE,{"disambiguationData":[OSD([sQuery(id+"F0.wireOp",EDGE,"E1"),sQuery(id+"F0.wireOp",EDGE,"E2")])]});
            var Q9;
            Q9=makeQuery(id+"F3.opFillet","BLEND_EDGE",EDGE,{"blendedFrom":[makeQuery(id+"F1.opExtrude","CAP_EDGE",EDGE,{"disambiguationData":[OSD([sQuery(id+"F0.wireOp",EDGE,"E2")])],"isStart":false}),makeQuery(id+"F1.opExtrude","SWEPT_FACE",FACE,{"disambiguationData":[OSD([sQuery(id+"F0.wireOp",EDGE,"E1")])]})],"blendedInto":[makeQuery(id+"F1.opExtrude","SWEPT_FACE",FACE,{"disambiguationData":[OSD([sQuery(id+"F0.wireOp",EDGE,"E1")])]})]});
            var Q10;
            Q10=makeQuery(id+"F1.opExtrude","CAP_EDGE",EDGE,{"disambiguationData":[OSD([sQuery(id+"F0.wireOp",EDGE,"E10.filletArc")])],"isStart":false});
            var Q11;
            Q11=makeQuery(id+"F3.opFillet","BLEND_EDGE",EDGE,{"blendedFrom":[makeQuery(id+"F1.opExtrude","CAP_EDGE",EDGE,{"disambiguationData":[OSD([sQuery(id+"F0.wireOp",EDGE,"E2")])],"isStart":false}),makeQuery(id+"F1.opExtrude","SWEPT_FACE",FACE,{"disambiguationData":[OSD([sQuery(id+"F0.wireOp",EDGE,"E10.filletArc")])]})],"blendedInto":[makeQuery(id+"F1.opExtrude","SWEPT_FACE",FACE,{"disambiguationData":[OSD([sQuery(id+"F0.wireOp",EDGE,"E10.filletArc")])]})]});
            var Q12;
            {var subQ0=sQuery(id+"F0.wireOp",EDGE,"E2");Q12=makeQuery(id+"F3.opFillet","BLEND_EDGE",EDGE,{"blendedFrom":[makeQuery(id+"F2.opShell","OFFSET_EDGE",EDGE,{"disambiguationData":[OSD([subQ0]),TDD([makeQuery(id+"F1.opExtrude","CAP_EDGE",EDGE,{"disambiguationData":[OSD([subQ0])],"isStart":false})])]}),makeQuery(id+"F1.opExtrude","SWEPT_FACE",FACE,{"disambiguationData":[OSD([sQuery(id+"F0.wireOp",EDGE,"E10.filletArc")])]})],"blendedInto":[makeQuery(id+"F1.opExtrude","SWEPT_FACE",FACE,{"disambiguationData":[OSD([sQuery(id+"F0.wireOp",EDGE,"E10.filletArc")])]})]});}
            var Q13;
            {var subQ0=sQuery(id+"F0.wireOp",EDGE,"E10.filletArc");Q13=makeQuery(id+"F2.opShell","OFFSET_EDGE",EDGE,{"disambiguationData":[OSD([subQ0]),TDD([makeQuery(id+"F1.opExtrude","CAP_EDGE",EDGE,{"disambiguationData":[OSD([subQ0])],"isStart":false})])]});}
            var Q14;
            {var subQ0=sQuery(id+"F0.wireOp",EDGE,"E2");Q14=makeQuery(id+"F3.opFillet","BLEND_EDGE",EDGE,{"blendedFrom":[makeQuery(id+"F2.opShell","OFFSET_EDGE",EDGE,{"disambiguationData":[OSD([subQ0]),TDD([makeQuery(id+"F1.opExtrude","CAP_EDGE",EDGE,{"disambiguationData":[OSD([subQ0])],"isStart":false})])]}),makeQuery(id+"F1.opExtrude","SWEPT_FACE",FACE,{"disambiguationData":[OSD([sQuery(id+"F0.wireOp",EDGE,"E1")])]})],"blendedInto":[makeQuery(id+"F1.opExtrude","SWEPT_FACE",FACE,{"disambiguationData":[OSD([sQuery(id+"F0.wireOp",EDGE,"E1")])]})]});}
            var Q15;
            Q15=makeQuery(id+"F2.opShell","OFFSET_EDGE",EDGE,{"disambiguationData":[OSD([sQuery(id+"F0.wireOp",EDGE,"E1"),sQuery(id+"F0.wireOp",EDGE,"E2")])]});
            var Q16;
            {var subQ0=sQuery(id+"F0.wireOp",EDGE,"E9");Q16=makeQuery(id+"F2.opShell","OFFSET_EDGE",EDGE,{"disambiguationData":[OSD([subQ0]),TDD([makeQuery(id+"F1.opExtrude","CAP_EDGE",EDGE,{"disambiguationData":[OSD([subQ0])],"isStart":false})])]});}
            var Q17;
            Q17=makeQuery(id+"F2.opShell","OFFSET_EDGE",EDGE,{"disambiguationData":[OSD([sQuery(id+"F0.wireOp",EDGE,"E0"),sQuery(id+"F0.wireOp",EDGE,"E9")])]});
            var Q18;
            {var subQ0=sQuery(id+"F0.wireOp",EDGE,"E0");Q18=makeQuery(id+"F3.opFillet","BLEND_EDGE",EDGE,{"blendedFrom":[makeQuery(id+"F2.opShell","OFFSET_EDGE",EDGE,{"disambiguationData":[OSD([subQ0]),TDD([makeQuery(id+"F1.opExtrude","CAP_EDGE",EDGE,{"disambiguationData":[OSD([subQ0])],"isStart":false})])]}),makeQuery(id+"F1.opExtrude","SWEPT_FACE",FACE,{"disambiguationData":[OSD([sQuery(id+"F0.wireOp",EDGE,"E9")])]})],"blendedInto":[makeQuery(id+"F1.opExtrude","SWEPT_FACE",FACE,{"disambiguationData":[OSD([sQuery(id+"F0.wireOp",EDGE,"E9")])]})]});}
            var Q19;
            {var subQ0=sQuery(id+"F0.wireOp",EDGE,"E9");Q19=makeQuery(id+"F2.opShell","OFFSET_EDGE",EDGE,{"disambiguationData":[OSD([subQ0]),TDD([makeQuery(id+"F1.opExtrude","CAP_EDGE",EDGE,{"disambiguationData":[OSD([subQ0])],"isStart":true})])]});}
            var Q20;
            {var subQ0=sQuery(id+"F0.wireOp",EDGE,"E0");Q20=makeQuery(id+"F3.opFillet","BLEND_EDGE",EDGE,{"blendedFrom":[makeQuery(id+"F2.opShell","OFFSET_EDGE",EDGE,{"disambiguationData":[OSD([subQ0]),TDD([makeQuery(id+"F1.opExtrude","CAP_EDGE",EDGE,{"disambiguationData":[OSD([subQ0])],"isStart":true})])]}),makeQuery(id+"F1.opExtrude","SWEPT_FACE",FACE,{"disambiguationData":[OSD([sQuery(id+"F0.wireOp",EDGE,"E9")])]})],"blendedInto":[makeQuery(id+"F1.opExtrude","SWEPT_FACE",FACE,{"disambiguationData":[OSD([sQuery(id+"F0.wireOp",EDGE,"E9")])]})]});}
            var Q21;
            {var subQ0=sQuery(id+"F0.wireOp",EDGE,"E10.filletArc");Q21=makeQuery(id+"F2.opShell","OFFSET_EDGE",EDGE,{"disambiguationData":[OSD([subQ0]),TDD([makeQuery(id+"F1.opExtrude","CAP_EDGE",EDGE,{"disambiguationData":[OSD([subQ0])],"isStart":true})])]});}
            var Q22;
            {var subQ0=sQuery(id+"F0.wireOp",EDGE,"E2");Q22=makeQuery(id+"F3.opFillet","BLEND_EDGE",EDGE,{"blendedFrom":[makeQuery(id+"F2.opShell","OFFSET_EDGE",EDGE,{"disambiguationData":[OSD([subQ0]),TDD([makeQuery(id+"F1.opExtrude","CAP_EDGE",EDGE,{"disambiguationData":[OSD([subQ0])],"isStart":true})])]}),makeQuery(id+"F2.opShell","OFFSET_FACE",FACE,{"disambiguationData":[OSD([sQuery(id+"F0.wireOp",EDGE,"E10.filletArc")])]})],"blendedInto":[makeQuery(id+"F2.opShell","OFFSET_FACE",FACE,{"disambiguationData":[OSD([sQuery(id+"F0.wireOp",EDGE,"E10.filletArc")])]})]});}
            var Q23;
            {var subQ0=sQuery(id+"F0.wireOp",EDGE,"E2");Q23=makeQuery(id+"F3.opFillet","BLEND_EDGE",EDGE,{"blendedFrom":[makeQuery(id+"F2.opShell","OFFSET_EDGE",EDGE,{"disambiguationData":[OSD([subQ0]),TDD([makeQuery(id+"F1.opExtrude","CAP_EDGE",EDGE,{"disambiguationData":[OSD([subQ0])],"isStart":true})])]}),makeQuery(id+"F1.opExtrude","SWEPT_FACE",FACE,{"disambiguationData":[OSD([sQuery(id+"F0.wireOp",EDGE,"E1")])]})],"blendedInto":[makeQuery(id+"F1.opExtrude","SWEPT_FACE",FACE,{"disambiguationData":[OSD([sQuery(id+"F0.wireOp",EDGE,"E1")])]})]});}
            fillet(context, id + "F19", {"entities" : qUnion([Q0, Q1, Q2, Q3, Q4, Q5, Q6, Q7, Q8, Q9, Q10, Q11, Q12, Q13, Q14, Q15, Q16, Q17, Q18, Q19, Q20, Q21, Q22, Q23]), "radius" : 0.89 * mm, "tangentPropagation" : true, "allowEdgeOverflow" : false});
        }
    });
